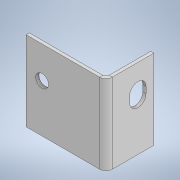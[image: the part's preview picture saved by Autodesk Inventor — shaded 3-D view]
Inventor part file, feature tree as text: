
AUTODESK INVENTOR PART (.ipt)
format: ipt  version: 2022 (Build 260153000, 153)  size: 139,264 bytes
history: native  units: mm
features: sheet_metal_op x3, sketch x3, extrude x2, other x1
ambient origin geometry x8: Origin, YZ Plane, XZ Plane, XY Plane, X Axis, Y Axis, Z Axis, Center Point
bodies: Solid1 (feature_tree)
feature tree (9):
  sheet_metal_op  "Contour Flange1"
  extrude  "Extrusion1"  Depth=50.0mm
  extrude  "Extrusion2"  Depth=2.0mm
  sketch  "Sketch1"  dims[d0=30.0mm d1=50.0mm]
  other  "Plate1"
  sheet_metal_op  "Bend1"
  sheet_metal_op  "Corner1"
  sketch  "Sketch2"  dims[d2=2.0mm d3=2.0mm]
  sketch  "Sketch3"  dims[d4=1.0mm d5=4.0mm d6=2.0mm d7=50.0mm d8=2.0mm d9=0.5mm d10=8.0mm d11=2.0mm d12=2.0mm d13=10.2mm d14=10.2mm d16=10.0mm d17=4.0mm d18=2.0mm d19=10.0mm d20=0.0mm d21=40.0mm d22=8.0mm d24=10.0mm d25=0.0mm d26=17.5mm d27=20.0mm]
